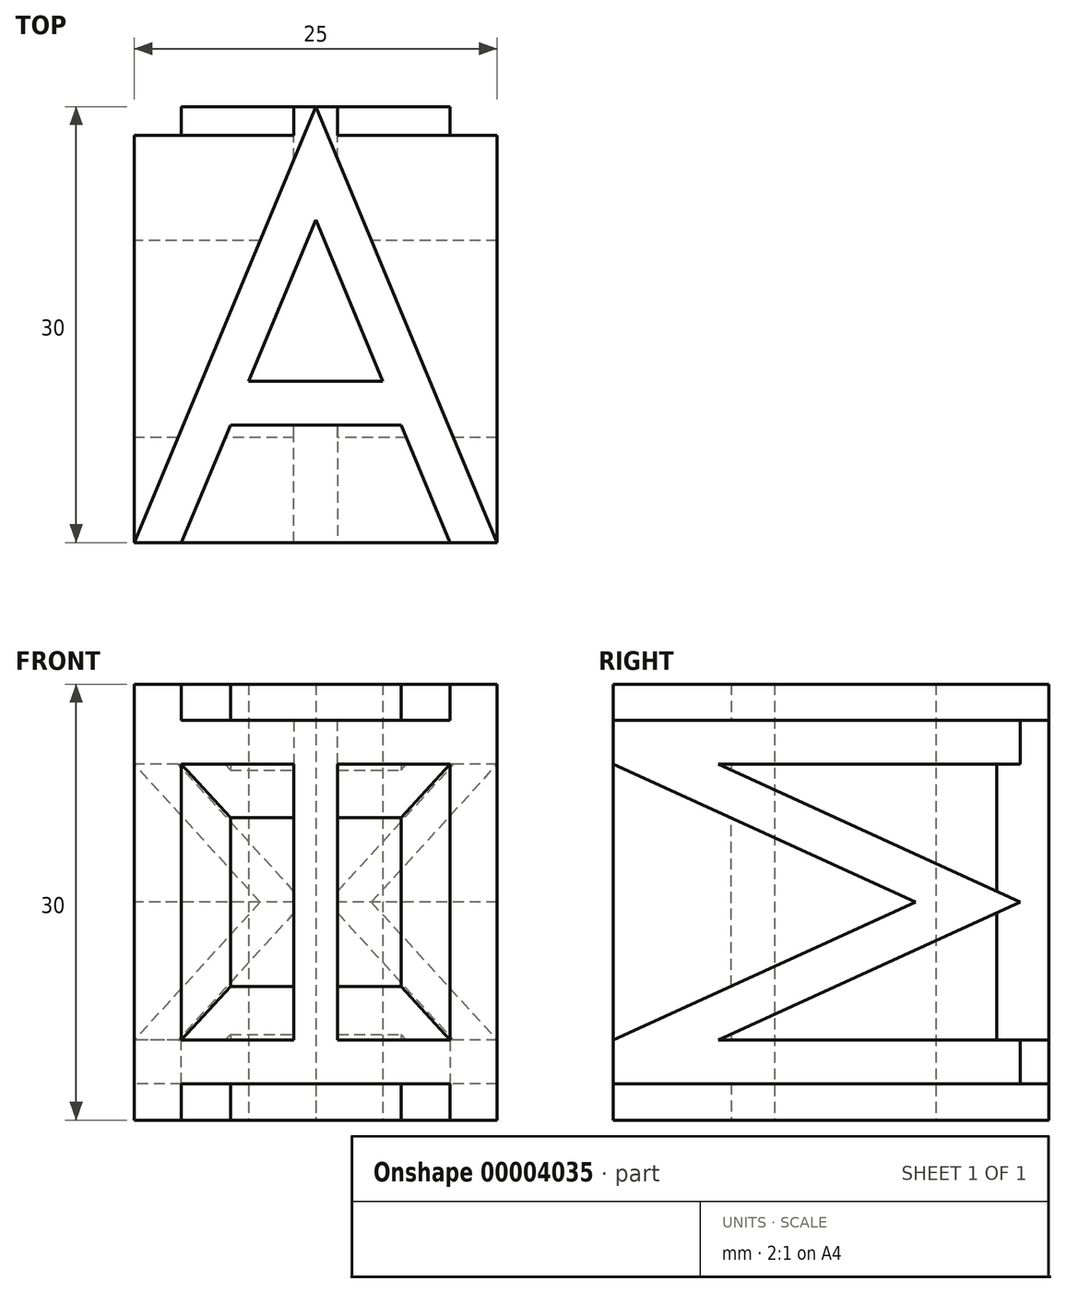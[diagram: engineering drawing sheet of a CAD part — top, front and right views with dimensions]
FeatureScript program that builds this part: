
annotation { "Feature Type Name" : "Feature", "Feature Type Description" : "" }
export const myFeature = defineFeature(function(context is Context, id is Id, definition is map)
    precondition{}
    {
        {
            var Q0;
            Q0=qCreatedBy(makeId("Top.planeOp"),FACE);
            var sketch = newSketch(context, id + "F0", { "sketchPlane" : qUnion([Q0])});
            skLineSegment(sketch, "E0.bottom", {"start": v(-12.5, 15) * mm, "end": v(12.5, 15) * mm, "construction": true});
            skLineSegment(sketch, "E0.top", {"start": v(-12.5, -15) * mm, "end": v(12.5, -15) * mm, "construction": true});
            skLineSegment(sketch, "E0.left", {"start": v(-12.5, 15) * mm, "end": v(-12.5, -15) * mm, "construction": true});
            skLineSegment(sketch, "E0.right", {"start": v(12.5, 15) * mm, "end": v(12.5, -15) * mm, "construction": true});
            skLineSegment(sketch, "E1", {"start": v(-12.5, 15) * mm, "end": v(12.5, -15) * mm, "construction": true});
            skLineSegment(sketch, "E2", {"start": v(-12.5, -15) * mm, "end": v(12.5, 15) * mm, "construction": true});
            skLineSegment(sketch, "E3", {"start": v(0, 15) * mm, "end": v(-12.5, -15) * mm});
            skLineSegment(sketch, "E4", {"start": v(0, 15) * mm, "end": v(12.5, -15) * mm});
            skLineSegment(sketch, "E5", {"start": v(-5.87, -6.9) * mm, "end": v(5.88, -6.9) * mm});
            skLineSegment(sketch, "E6.0", {"start": v(0, 7.2) * mm, "end": v(-4.63, -3.9) * mm});
            skLineSegment(sketch, "E6.1", {"start": v(0, 7.2) * mm, "end": v(4.63, -3.9) * mm});
            skLineSegment(sketch, "E7.0", {"start": v(-4.63, -3.9) * mm, "end": v(4.63, -3.9) * mm});
            skLineSegment(sketch, "E8", {"start": v(-12.5, -15) * mm, "end": v(-9.25, -15) * mm});
            skLineSegment(sketch, "E9", {"start": v(9.25, -15) * mm, "end": v(12.5, -15) * mm});
            skLineSegment(sketch, "E10.trimOffspring", {"start": v(-5.87, -6.9) * mm, "end": v(-9.25, -15) * mm});
            skLineSegment(sketch, "E11.trimOffspring", {"start": v(5.88, -6.9) * mm, "end": v(9.25, -15) * mm});
            skSolve(sketch);
        }
        {
            var Q0;
            Q0=makeQuery(id+"F0.imprint","IMPRINT",FACE,{"disambiguationData":[TD([[makeQuery(id+"F0.imprint","IMPRINT",EDGE,{"derivedFrom":sQuery(id+"F0.wireOp",EDGE,"E3")}),1.0]])]});
            extrude(context, id + "F1", {"entities" : qUnion([Q0]), "endBound" : BoundingType.SYMMETRIC, "depth" : 30 * mm});
        }
        {
            var Q0;
            Q0=qCreatedBy(makeId("Right.planeOp"),FACE);
            var sketch = newSketch(context, id + "F2", { "sketchPlane" : qUnion([Q0])});
            skLineSegment(sketch, "E12", {"start": v(-15, -12.5) * mm, "end": v(-15, -9.5) * mm});
            skLineSegment(sketch, "E13", {"start": v(-15, -9.5) * mm, "end": v(5.8, 0) * mm});
            skLineSegment(sketch, "E14", {"start": v(13.02, -12.5) * mm, "end": v(13.02, -9.5) * mm});
            skLineSegment(sketch, "E15", {"start": v(13.02, -9.5) * mm, "end": v(-7.78, -9.5) * mm});
            skLineSegment(sketch, "E16", {"start": v(-7.78, -9.5) * mm, "end": v(13.02, 0) * mm});
            skLineSegment(sketch, "E17.0.MirrorCS", {"start": v(-15, 9.5) * mm, "end": v(5.8, 0) * mm});
            skLineSegment(sketch, "E18.0.MirrorCS", {"start": v(-15, 12.5) * mm, "end": v(-15, 9.5) * mm});
            skLineSegment(sketch, "E19.0.MirrorCS", {"start": v(13.02, 12.5) * mm, "end": v(13.02, 9.5) * mm});
            skLineSegment(sketch, "E20.0.MirrorCS", {"start": v(13.02, 9.5) * mm, "end": v(-7.78, 9.5) * mm});
            skLineSegment(sketch, "E21.0.MirrorCS", {"start": v(-7.78, 9.5) * mm, "end": v(13.02, 0) * mm});
            skLineSegment(sketch, "E22", {"start": v(13.02, -12.5) * mm, "end": v(-15, -12.5) * mm});
            skLineSegment(sketch, "E23", {"start": v(13.02, 12.5) * mm, "end": v(-15, 12.5) * mm});
            skLineSegment(sketch, "E24", {"start": v(13.02, 9.5) * mm, "end": v(13.02, -9.5) * mm, "construction": true});
            skSolve(sketch);
        }
        {
            var Q0;
            Q0=makeQuery(id+"F2.imprint","IMPRINT",FACE,{"disambiguationData":[TD([[makeQuery(id+"F2.imprint","IMPRINT",EDGE,{"derivedFrom":sQuery(id+"F2.wireOp",EDGE,"E13")}),-1.0]])]});
            extrude(context, id + "F3", {"entities" : qUnion([Q0]), "operationType" : NewBodyOperationType.ADD, "endBound" : BoundingType.SYMMETRIC, "depth" : 25 * mm});
        }
        {
            var Q0;
            Q0=qCreatedBy(makeId("Front.planeOp"),FACE);
            var sketch = newSketch(context, id + "F4", { "sketchPlane" : qUnion([Q0])});
            skLineSegment(sketch, "E25.0", {"start": v(9.25, -12.5) * mm, "end": v(-9.25, -12.5) * mm});
            skLineSegment(sketch, "E25.1", {"start": v(9.25, 12.5) * mm, "end": v(-9.25, 12.5) * mm});
            skLineSegment(sketch, "E26", {"start": v(9.25, -12.5) * mm, "end": v(9.25, -9.5) * mm});
            skLineSegment(sketch, "E27", {"start": v(9.25, -9.5) * mm, "end": v(1.5, -9.5) * mm});
            skLineSegment(sketch, "E28", {"start": v(1.5, -9.5) * mm, "end": v(1.5, 12.5) * mm});
            skLineSegment(sketch, "E29", {"start": v(1.5, 12.5) * mm, "end": v(-1.5, 12.5) * mm});
            skLineSegment(sketch, "E30", {"start": v(-1.5, 12.5) * mm, "end": v(-1.5, -9.5) * mm});
            skLineSegment(sketch, "E31", {"start": v(-1.5, -9.5) * mm, "end": v(-9.25, -9.5) * mm});
            skLineSegment(sketch, "E32", {"start": v(-9.25, -9.5) * mm, "end": v(-9.25, -12.5) * mm});
            skLineSegment(sketch, "E33", {"start": v(1.5, 0) * mm, "end": v(-1.5, 0) * mm, "construction": true});
            skSolve(sketch);
        }
        {
            var Q0;
            Q0=makeQuery(id+"F4.imprint","IMPRINT",FACE,{"disambiguationData":[TD([[makeQuery(id+"F4.imprint","IMPRINT",EDGE,{"derivedFrom":sQuery(id+"F4.wireOp",EDGE,"E25.0")}),-1.0]])]});
            extrude(context, id + "F5", {"entities" : qUnion([Q0]), "operationType" : NewBodyOperationType.ADD, "endBound" : BoundingType.SYMMETRIC, "depth" : 30 * mm});
        }
        {
            var Q0;
            Q0=makeQuery(id+"F3.boolean.opBoolean","SPLIT",FACE,{"disambiguationData":[TD([makeQuery(id+"F1.opExtrude","SWEPT_FACE",FACE,{"disambiguationData":[OSD([sQuery(id+"F0.wireOp",EDGE,"E6.0")])]})])],"derivedFrom":makeQuery(id+"F3.opExtrude","SWEPT_FACE",FACE,{"disambiguationData":[OSD([sQuery(id+"F2.wireOp",EDGE,"E23")])]})});
            extrude(context, id + "F6", {"entities" : qUnion([Q0]), "operationType" : NewBodyOperationType.REMOVE, "endBound" : BoundingType.THROUGH_ALL, "oppositeDirection" : true, "depth" : 25 * mm});
        }
    });
